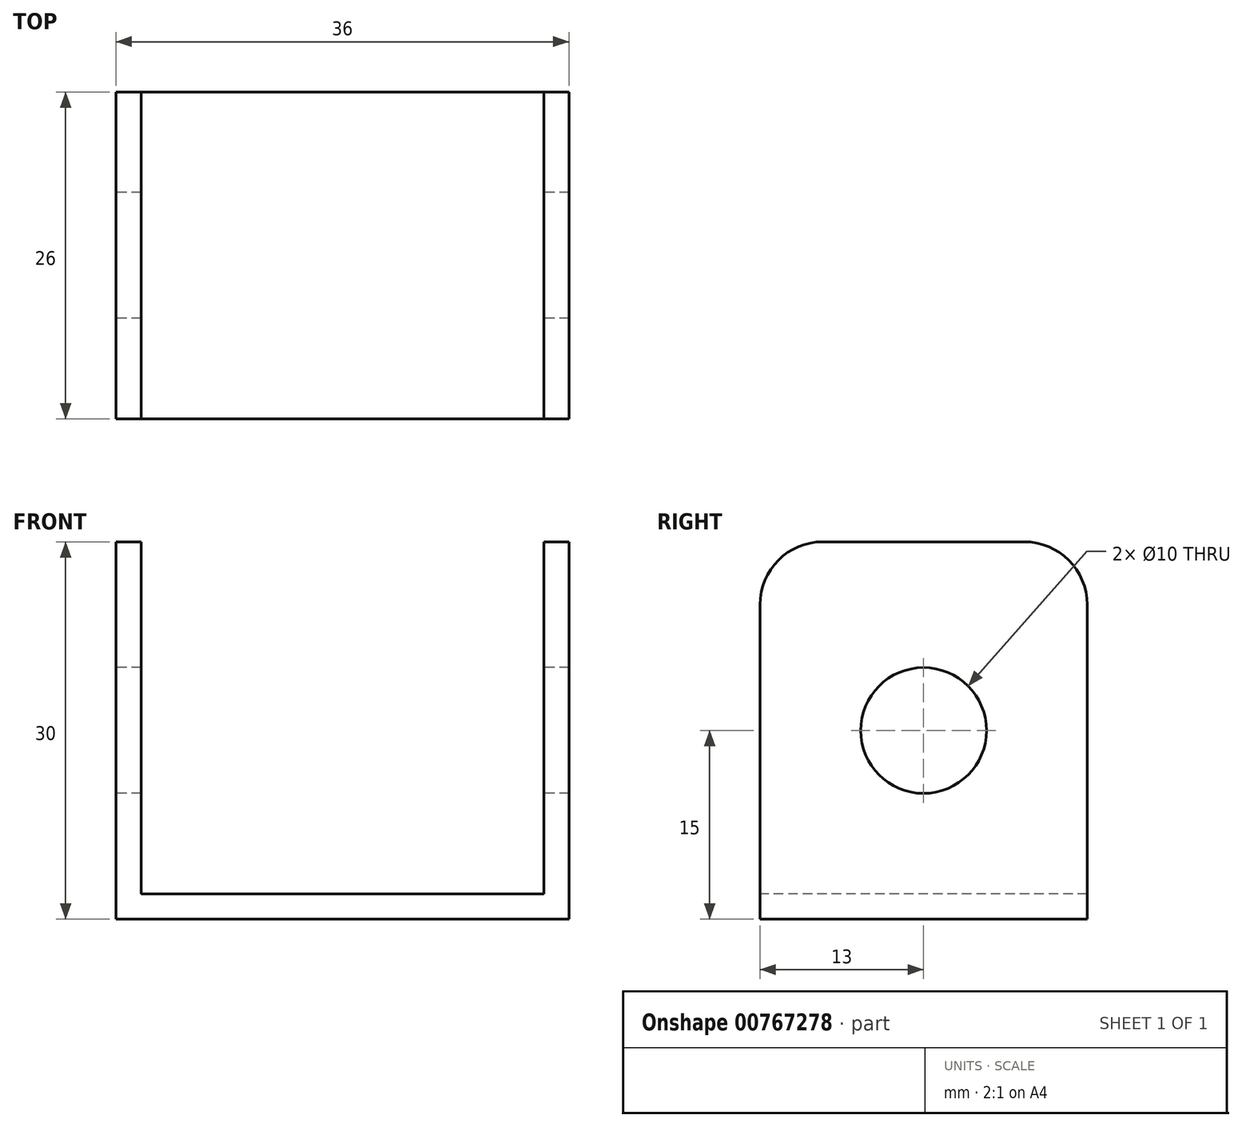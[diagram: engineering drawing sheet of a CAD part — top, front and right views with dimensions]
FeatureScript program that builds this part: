
annotation { "Feature Type Name" : "Feature", "Feature Type Description" : "" }
export const myFeature = defineFeature(function(context is Context, id is Id, definition is map)
    precondition{}
    {
        {
            var Q0;
            Q0=qCreatedBy(makeId("Top.planeOp"),FACE);
            var sketch = newSketch(context, id + "F0", { "sketchPlane" : qUnion([Q0])});
            skLineSegment(sketch, "E0.bottom", {"start": v(18, -13) * mm, "end": v(-18, -13) * mm});
            skLineSegment(sketch, "E0.top", {"start": v(18, 13) * mm, "end": v(-18, 13) * mm});
            skLineSegment(sketch, "E0.left", {"start": v(18, -13) * mm, "end": v(18, 13) * mm});
            skLineSegment(sketch, "E0.right", {"start": v(-18, -13) * mm, "end": v(-18, 13) * mm});
            skPoint(sketch, "E0.middle", {"position": v(0, 0) * mm});
            skLineSegment(sketch, "E1", {"start": v(-16, 13) * mm, "end": v(-16, -13) * mm});
            skLineSegment(sketch, "E2", {"start": v(16, 13) * mm, "end": v(16, -13) * mm});
            skSolve(sketch);
        }
        {
            var Q0;
            {var subQ0=sQuery(id+"F0.wireOp",EDGE,"E1");Q0=makeQuery(id+"F0.imprint","IMPRINT",FACE,{"disambiguationData":[TD([[makeQuery(id+"F0.imprint","IMPRINT",EDGE,{"derivedFrom":subQ0}),1.0]])]});}
            var Q1;
            {var subQ0=sQuery(id+"F0.wireOp",EDGE,"E0.right");Q1=makeQuery(id+"F0.imprint","IMPRINT",FACE,{"disambiguationData":[TD([[makeQuery(id+"F0.imprint","IMPRINT",EDGE,{"derivedFrom":subQ0}),-1.0]])]});}
            var Q2;
            {var subQ0=sQuery(id+"F0.wireOp",EDGE,"E0.left");Q2=makeQuery(id+"F0.imprint","IMPRINT",FACE,{"disambiguationData":[TD([[makeQuery(id+"F0.imprint","IMPRINT",EDGE,{"derivedFrom":subQ0}),1.0]])]});}
            extrude(context, id + "F1", {"entities" : qUnion([Q0, Q1, Q2]), "oppositeDirection" : true, "depth" : 2 * mm, "offsetDistance" : 25 * mm});
        }
        {
            var Q0;
            {var subQ0=sQuery(id+"F0.wireOp",EDGE,"E0.left");Q0=makeQuery(id+"F0.imprint","IMPRINT",FACE,{"disambiguationData":[TD([[makeQuery(id+"F0.imprint","IMPRINT",EDGE,{"derivedFrom":subQ0}),1.0]])]});}
            var Q1;
            {var subQ0=sQuery(id+"F0.wireOp",EDGE,"E0.right");Q1=makeQuery(id+"F0.imprint","IMPRINT",FACE,{"disambiguationData":[TD([[makeQuery(id+"F0.imprint","IMPRINT",EDGE,{"derivedFrom":subQ0}),-1.0]])]});}
            extrude(context, id + "F2", {"entities" : qUnion([Q0, Q1]), "operationType" : NewBodyOperationType.ADD, "depth" : 28 * mm, "offsetDistance" : 25 * mm});
        }
        {
            var Q0;
            {var subQ0=sQuery(id+"F0.wireOp",EDGE,"E0.right");Q0=makeQuery(id+"F2.boolean.opBoolean","MERGE",FACE,{"derivedFrom":[makeQuery(id+"F1.opExtrude","SWEPT_FACE",FACE,{"disambiguationData":[OSD([subQ0])]}),makeQuery(id+"F2.opExtrude","SWEPT_FACE",FACE,{"disambiguationData":[OSD([subQ0])]})]});}
            var sketch = newSketch(context, id + "F3", { "sketchPlane" : qUnion([Q0])});
            skCircle(sketch, "E3", {"center": v(0, 13) * mm, "radius": 5 * mm});
            skSolve(sketch);
        }
        {
            var Q0;
            Q0 = qSketchRegion(id + "F3", true);
            extrude(context, id + "F4", {"entities" : qUnion([Q0]), "operationType" : NewBodyOperationType.REMOVE, "oppositeDirection" : true, "depth" : 50 * mm, "offsetDistance" : 25 * mm});
        }
        {
            var Q0;
            {var subQ0=sQuery(id+"F0.wireOp",EDGE,"E0.top");Q0=makeQuery(id+"F2.opExtrude","CAP_EDGE",EDGE,{"disambiguationData":[OSD([subQ0]),TDD([makeQuery(id+"F0.imprint","IMPRINT",EDGE,{"disambiguationData":[TD([[makeQuery(id+"F0.imprint","INTERSECT",VERTEX,{"derivedFrom":[subQ0,sQuery(id+"F0.wireOp",EDGE,"E0.right")]}),1.0]])],"derivedFrom":subQ0})])],"isStart":false});}
            var Q1;
            {var subQ0=sQuery(id+"F0.wireOp",EDGE,"E0.top");Q1=makeQuery(id+"F2.opExtrude","CAP_EDGE",EDGE,{"disambiguationData":[OSD([subQ0]),TDD([makeQuery(id+"F0.imprint","IMPRINT",EDGE,{"disambiguationData":[TD([[makeQuery(id+"F0.imprint","INTERSECT",VERTEX,{"derivedFrom":[subQ0,sQuery(id+"F0.wireOp",EDGE,"E0.left")]}),-1.0]])],"derivedFrom":subQ0})])],"isStart":false});}
            var Q2;
            {var subQ0=sQuery(id+"F0.wireOp",EDGE,"E0.bottom");Q2=makeQuery(id+"F2.opExtrude","CAP_EDGE",EDGE,{"disambiguationData":[OSD([subQ0]),TDD([makeQuery(id+"F0.imprint","IMPRINT",EDGE,{"disambiguationData":[TD([[makeQuery(id+"F0.imprint","INTERSECT",VERTEX,{"derivedFrom":[subQ0,sQuery(id+"F0.wireOp",EDGE,"E0.left")]}),-1.0]])],"derivedFrom":subQ0})])],"isStart":false});}
            var Q3;
            {var subQ0=sQuery(id+"F0.wireOp",EDGE,"E0.bottom");Q3=makeQuery(id+"F2.opExtrude","CAP_EDGE",EDGE,{"disambiguationData":[OSD([subQ0]),TDD([makeQuery(id+"F0.imprint","IMPRINT",EDGE,{"disambiguationData":[TD([[makeQuery(id+"F0.imprint","INTERSECT",VERTEX,{"derivedFrom":[subQ0,sQuery(id+"F0.wireOp",EDGE,"E0.right")]}),1.0]])],"derivedFrom":subQ0})])],"isStart":false});}
            fillet(context, id + "F5", {"entities" : qUnion([Q0, Q1, Q2, Q3]), "radius" : 5 * mm, "tangentPropagation" : true, "allowEdgeOverflow" : false});
        }
    });
